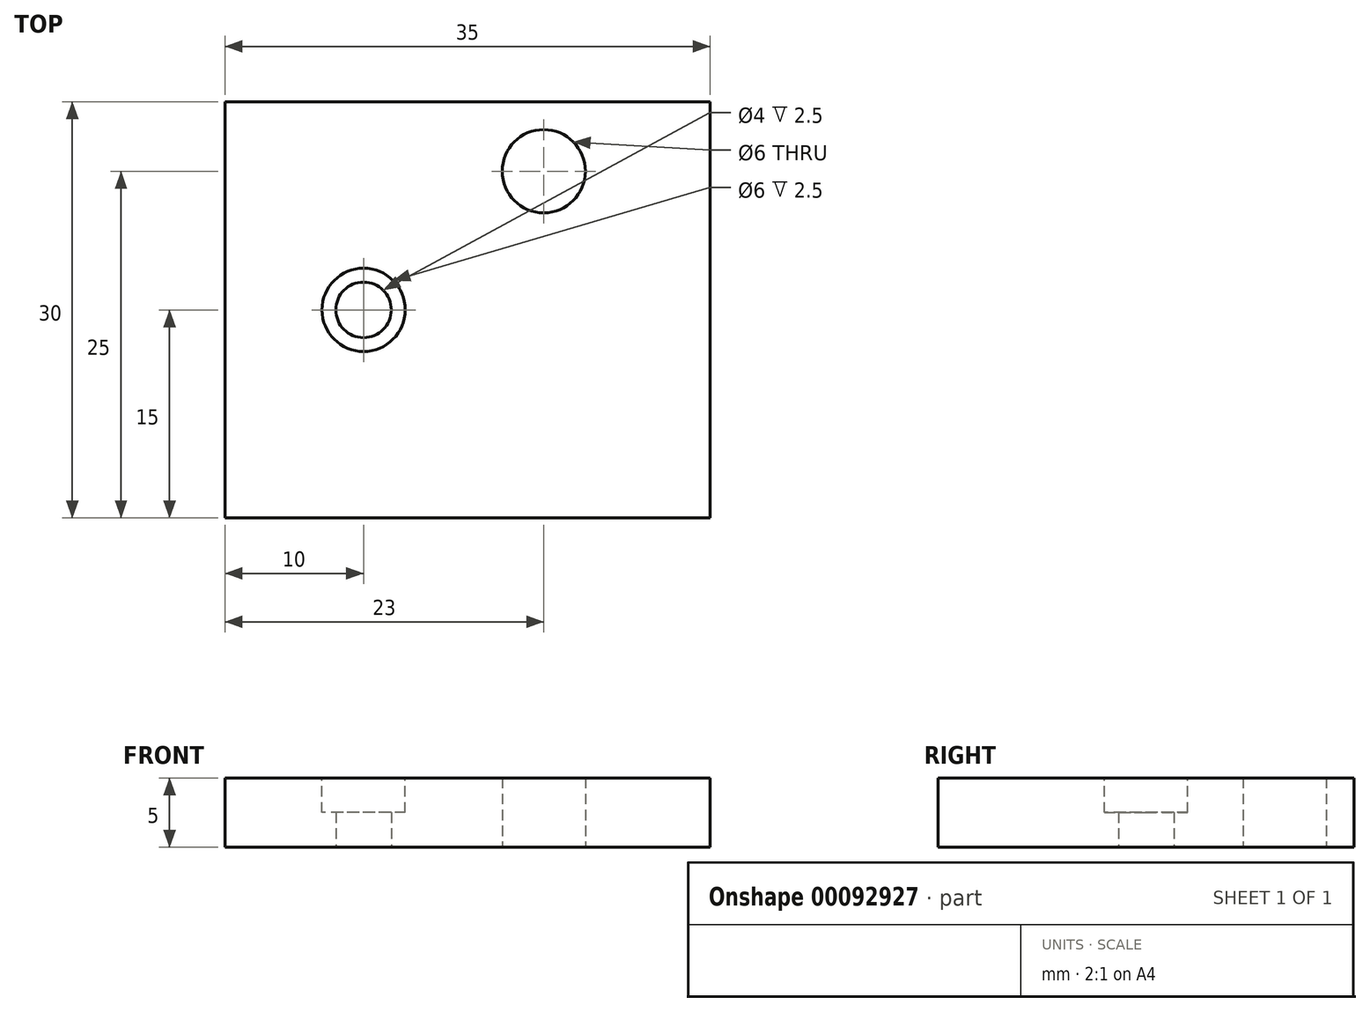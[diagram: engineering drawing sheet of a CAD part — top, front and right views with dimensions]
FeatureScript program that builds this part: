
annotation { "Feature Type Name" : "Feature", "Feature Type Description" : "" }
export const myFeature = defineFeature(function(context is Context, id is Id, definition is map)
    precondition{}
    {
        {
            var Q0;
            Q0=qCreatedBy(makeId("Top.planeOp"),FACE);
            var sketch = newSketch(context, id + "F0", { "sketchPlane" : qUnion([Q0])});
            skLineSegment(sketch, "E0.bottom", {"start": v(17.5, -15) * mm, "end": v(-17.5, -15) * mm});
            skLineSegment(sketch, "E0.top", {"start": v(17.5, 15) * mm, "end": v(-17.5, 15) * mm});
            skLineSegment(sketch, "E0.left", {"start": v(17.5, -15) * mm, "end": v(17.5, 15) * mm});
            skLineSegment(sketch, "E0.right", {"start": v(-17.5, -15) * mm, "end": v(-17.5, 15) * mm});
            skPoint(sketch, "E0.middle", {"position": v(0, 0) * mm});
            skCircle(sketch, "E1", {"center": v(-7.5, 0) * mm, "radius": 2 * mm});
            skCircle(sketch, "E2", {"center": v(5.5, 10) * mm, "radius": 3 * mm});
            skSolve(sketch);
        }
        {
            var Q0;
            Q0 = qSketchRegion(id + "F0", true);
            extrude(context, id + "F1", {"entities" : qUnion([Q0]), "depth" : 5 * mm});
        }
        {
            var Q0;
            Q0=makeQuery(id+"F1.opExtrude","CAP_FACE",FACE,{"disambiguationData":[OSD([sQuery(id+"F0.wireOp",EDGE,"E0.bottom"),sQuery(id+"F0.wireOp",EDGE,"E0.top"),sQuery(id+"F0.wireOp",EDGE,"E0.left"),sQuery(id+"F0.wireOp",EDGE,"E0.right"),sQuery(id+"F0.wireOp",EDGE,"E1"),sQuery(id+"F0.wireOp",EDGE,"E2")])],"isStart":false});
            var sketch = newSketch(context, id + "F2", { "sketchPlane" : qUnion([Q0])});
            skCircle(sketch, "E3", {"center": v(-7.5, 0) * mm, "radius": 3 * mm});
            skSolve(sketch);
        }
        {
            var Q0;
            Q0 = qSketchRegion(id + "F2", true);
            extrude(context, id + "F3", {"entities" : qUnion([Q0]), "operationType" : NewBodyOperationType.REMOVE, "oppositeDirection" : true, "depth" : 2.5 * mm});
        }
    });
